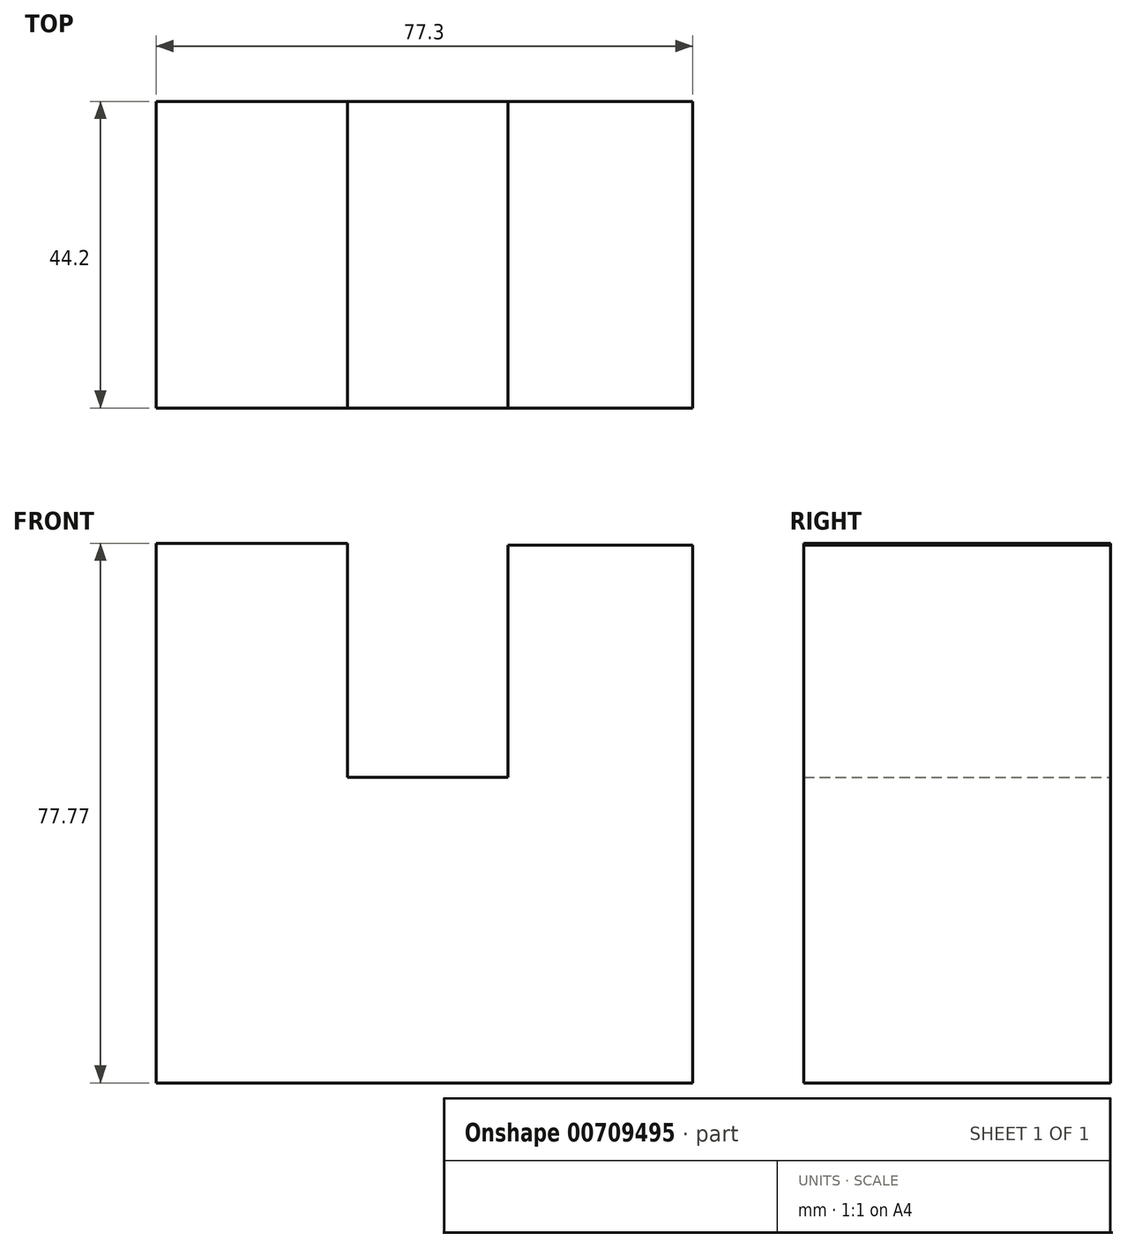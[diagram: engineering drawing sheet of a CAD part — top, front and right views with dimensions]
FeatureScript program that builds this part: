
annotation { "Feature Type Name" : "Feature", "Feature Type Description" : "" }
export const myFeature = defineFeature(function(context is Context, id is Id, definition is map)
    precondition{}
    {
        {
            var Q0;
            Q0=qCreatedBy(makeId("Front.planeOp"),FACE);
            var sketch = newSketch(context, id + "F0", { "sketchPlane" : qUnion([Q0])});
            skLineSegment(sketch, "E0", {"start": v(-63.28, 64.57) * mm, "end": v(-63.28, -13.2) * mm});
            skLineSegment(sketch, "E1", {"start": v(-63.28, -13.2) * mm, "end": v(14.02, -13.2) * mm});
            skLineSegment(sketch, "E2", {"start": v(14.02, -13.2) * mm, "end": v(14.02, 64.34) * mm});
            skLineSegment(sketch, "E3", {"start": v(14.02, 64.34) * mm, "end": v(-12.6, 64.34) * mm});
            skLineSegment(sketch, "E4", {"start": v(-12.6, 64.34) * mm, "end": v(-12.6, 30.87) * mm});
            skLineSegment(sketch, "E5", {"start": v(-12.6, 30.87) * mm, "end": v(-35.7, 30.87) * mm});
            skLineSegment(sketch, "E6", {"start": v(-35.7, 30.87) * mm, "end": v(-35.7, 63.63) * mm});
            skLineSegment(sketch, "E7", {"start": v(-63.28, 64.57) * mm, "end": v(-35.7, 64.57) * mm});
            skLineSegment(sketch, "E8", {"start": v(-35.7, 64.57) * mm, "end": v(-35.7, 63.63) * mm});
            skSolve(sketch);
        }
        {
            var Q0;
            Q0 = qSketchRegion(id + "F0", true);
            extrude(context, id + "F1", {"entities" : qUnion([Q0]), "depth" : 44.2 * mm, "offsetDistance" : 25.4 * mm});
        }
    });
